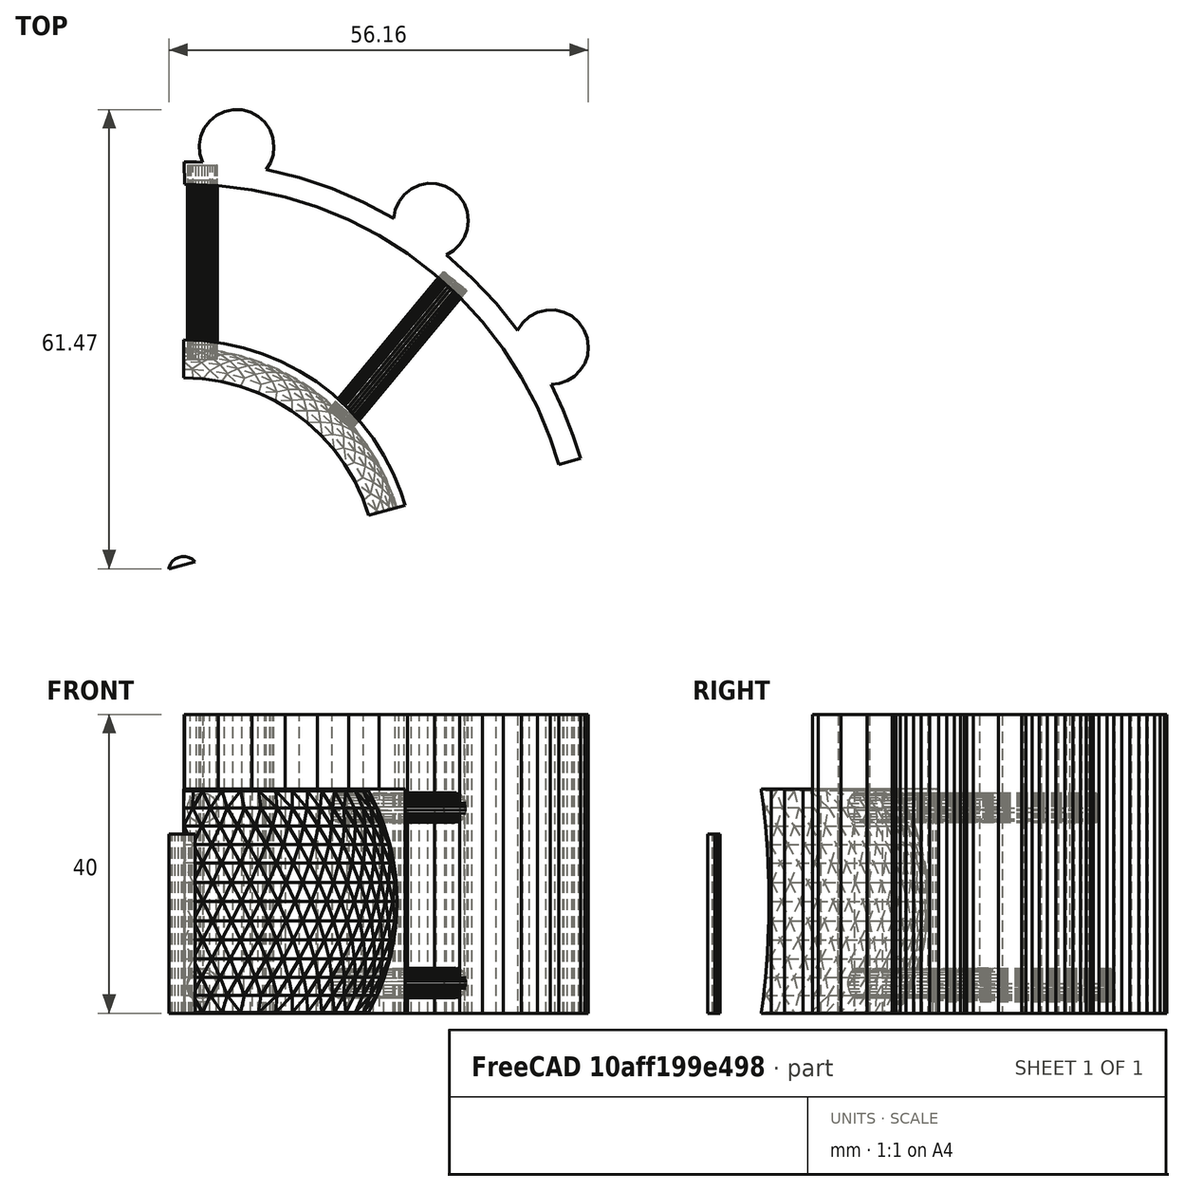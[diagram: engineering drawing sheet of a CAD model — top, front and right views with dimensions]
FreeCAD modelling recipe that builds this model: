
FCSTD DOCUMENT  (FreeCAD 1.1R43946 (Git))
Label: final_doornob_arc_small
License: All rights reserved
LicenseURL: https://en.wikipedia.org/wiki/All_rights_reserved
objects: Part::Feature×2, Mesh::Feature×1, Part::Box×1, Part::Cut×1
note: 4 computed .brp shape members not serialized (recipe doc carries the construction recipe); baked Part::Feature solids carry a one-line shape summary decoded from their .brp

FEATURE [Mesh::Feature] arthritis_door_handle_mk3
FEATURE [Part::Feature] arthritis_door_handle_mk001
  shape: bbox 64.29 x 63.81 x 40 mm, 1954 faces, 0 solids (baked)
FEATURE [Part::Feature] arthritis_door_handle_mk001_solid  label="arthritis_door_handle_mk001 (Solid)"
  shape: bbox 64.29 x 63.81 x 40 mm, 1954 faces (baked)
FEATURE [Part::Box] Box  label="Cube"
  AttacherType = Attacher::AttachEngine3D
  Height = 70
  Length = 99
  Placement = pos=(1.4235,-15.3126,-6.5) rot=(0,0,1;0.261799rad)
  Width = 16
FEATURE [Part::Cut] Cut
  Base = -> arthritis_door_handle_mk001_solid
  Refine = true
  Tool = -> Box
